# Revit family: spectral_aoca_aoca-p-l640_840-nd_d705
name_source: partatom
category: Lighting Fixtures
revit_build: Autodesk Revit 2016 (Build: 20150220_1215(x64)
units: mm (PartAtom-declared; Revit-internal decimal feet)

## family parameters
Cut with Voids When Loaded = No
Host = Face
Light Source = No
Part Type = Normal
Room Calculation Point = No
Round Connector Dimension = Use Diameter
Shared = No

## types (1)
- SPECTRAL AOCA (1 x )
    Apparent Load = 0 VA
    Approval mark = CE
    CIE Flux Codes = 16 40 69 50 76
    Control Gear = Electronic transformer
    Default Elevation = 1800 mm
    Description = SPF0620001
Surface-mounted downlighter

Design: 
Tubular shaped pendant LED luminaire. Luminaire body in UV-resistant PMMA formed as a hollow cylinder. LED lampholder fixed centrally in the luminaire
body using bright galvanised knurled screws. Lower tube opening closed by an opal PMMA panel using 4 knurled screws. Lampholder in white powdercoated steel fitted all round with 4 vertically arranged LED linear modules. LED linear circuit boards with colour rendering Ra >= 80, Standard colour tolerance < 3 Step Mac Adam (initial). Mid-Power LEDs for even illumination and maximum efficiency. 
Light colours 3000 K (…-830) or 4000 K (…-840).
Base profile in extruded aluminium for optimum thermal management. Linear circuit board continuously interlocked with base profile along the whole
length. Cover in clear, satinised or opal PMMA for efficient light emission. Pendant mounting using canopy in white powder coated steel. Canopy
accommodates all electrical components. Mechanical pendant connection using steel wire with 4-point fixture, electrical connection via transparent mains cable. Suspension height up to 1500 mm. Also in a dimmable version.
    Height = 640 mm  [stored 2.09974 ft]
    Lamp = 1 x
    Lamp count = 1
    Length = 200 mm  [stored 0.656168 ft]
    Luminous efficacy = 0 lm/W
    Manufacturer = Ridi
    ModVariant = No
    Model = AOCA-P-L640/840-ND
    Mounting Place = Ceiling
    Mounting Type = Pendant
    Number of Poles = 1
    OnlyDefault = Yes
    Power Factor = 1
    Product Name = SPECTRAL AOCA
    Product group = Pendant luminaire
    ProductGroupID = 9
    Protection Class = Protection class
    Protection Degree = IP 20
    RlxData = <blob elided: 18497 chars, md5=d3bca0e4>
    Socket = socket
    Standby Power = 0 W
    System Light Flux = 0 lm
    System Power = 0 W
    Type Image = aoca.jpg
    URL = http://reluxnet.relux.com
    VarID = 1
    Voltage = 0 V
    Weight = 0.00 kg
    Width = 0 mm  [stored 0 ft]

note: [stored X ft] marks values corroborated as IEEE doubles in the binary element streams (Revit-internal decimal feet)

## geometry (parser evidence)
native form markers: Blend x4, Sweep x12
no freeform markers — native parametric forms only
